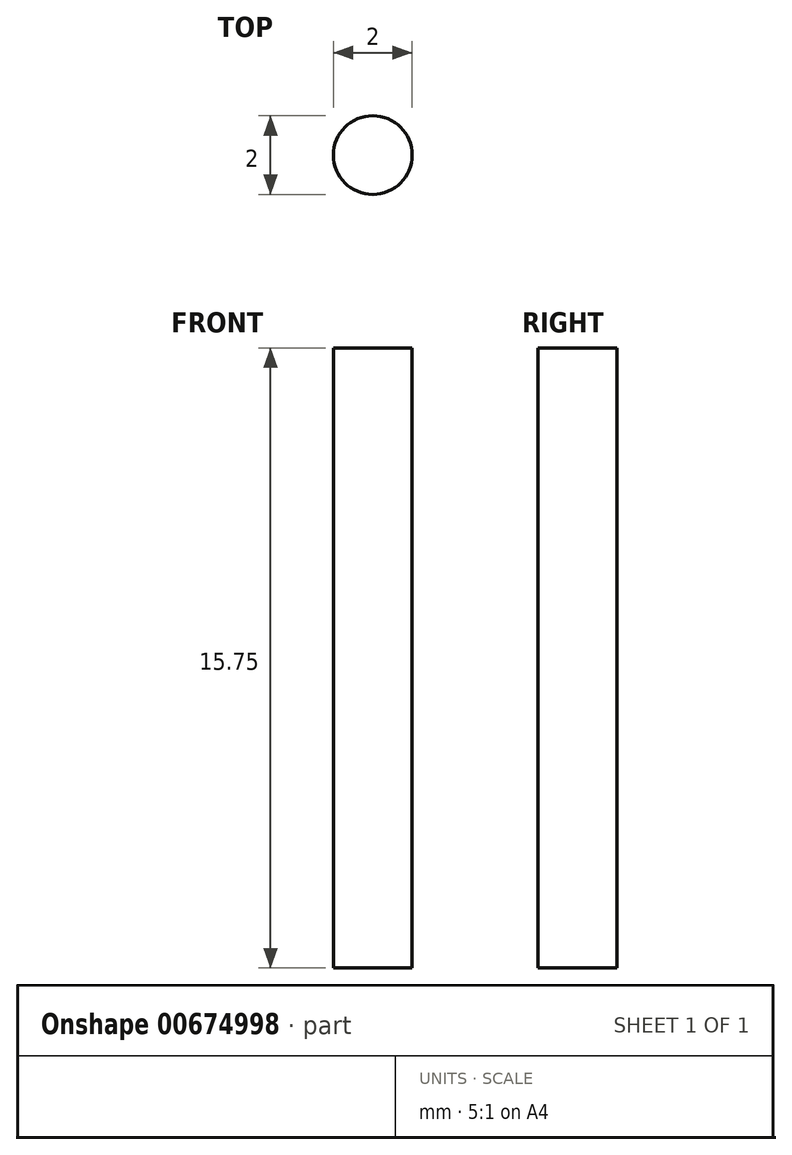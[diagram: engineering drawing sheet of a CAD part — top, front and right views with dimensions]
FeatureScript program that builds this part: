
annotation { "Feature Type Name" : "Feature", "Feature Type Description" : "" }
export const myFeature = defineFeature(function(context is Context, id is Id, definition is map)
    precondition{}
    {
        {
            assignVariable(context, id + "F0", {"name" : "Faktor", "anyValue" : 1.5});
        }
        {
            var Q0;
            Q0=qCreatedBy(makeId("Top.planeOp"),FACE);
            var sketch = newSketch(context, id + "F1", { "sketchPlane" : qUnion([Q0])});
            skCircle(sketch, "E0", {"center": v(0, 0) * mm, "radius": 1 * mm});
            skSolve(sketch);
        }
        {
            var Q0;
            Q0=qSketchRegion(id+"F1",true);
            extrude(context, id + "F2", {"entities" : qUnion([Q0]), "depth" : getVariable(context, 'Faktor') * 10.5 * mm, "offsetDistance" : 25 * mm});
        }
    });
